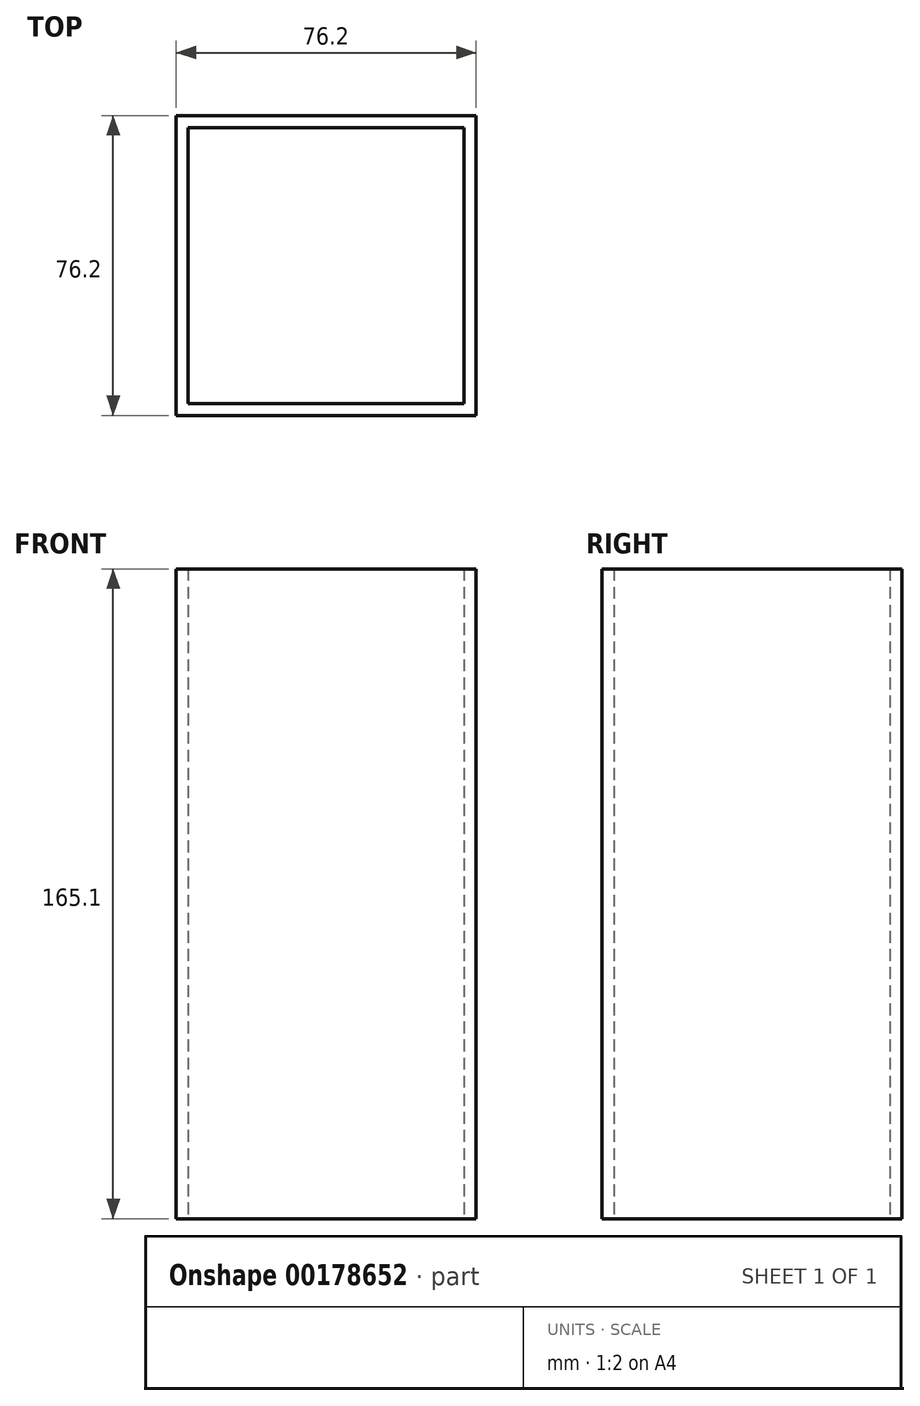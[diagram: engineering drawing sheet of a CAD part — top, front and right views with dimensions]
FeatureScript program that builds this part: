
annotation { "Feature Type Name" : "Feature", "Feature Type Description" : "" }
export const myFeature = defineFeature(function(context is Context, id is Id, definition is map)
    precondition{}
    {
        {
            var Q0;
            Q0=qCreatedBy(makeId("Top.planeOp"),FACE);
            var sketch = newSketch(context, id + "F0", { "sketchPlane" : qUnion([Q0])});
            skLineSegment(sketch, "E0.bottom", {"start": v(38.1, 38.1) * mm, "end": v(-38.1, 38.1) * mm});
            skLineSegment(sketch, "E0.top", {"start": v(38.1, -38.1) * mm, "end": v(-38.1, -38.1) * mm});
            skLineSegment(sketch, "E0.left", {"start": v(38.1, 38.1) * mm, "end": v(38.1, -38.1) * mm});
            skLineSegment(sketch, "E0.right", {"start": v(-38.1, 38.1) * mm, "end": v(-38.1, -38.1) * mm});
            skPoint(sketch, "E0.middle", {"position": v(0, 0) * mm});
            skLineSegment(sketch, "E1.bottom", {"start": v(35.05, 35.05) * mm, "end": v(-35.05, 35.05) * mm});
            skLineSegment(sketch, "E1.top", {"start": v(35.05, -35.05) * mm, "end": v(-35.05, -35.05) * mm});
            skLineSegment(sketch, "E1.left", {"start": v(35.05, 35.05) * mm, "end": v(35.05, -35.05) * mm});
            skLineSegment(sketch, "E1.right", {"start": v(-35.05, 35.05) * mm, "end": v(-35.05, -35.05) * mm});
            skSolve(sketch);
        }
        {
            var Q0;
            Q0 = qSketchRegion(id + "F0", true);
            extrude(context, id + "F1", {"entities" : qUnion([Q0]), "depth" : 165.1 * mm});
        }
    });
